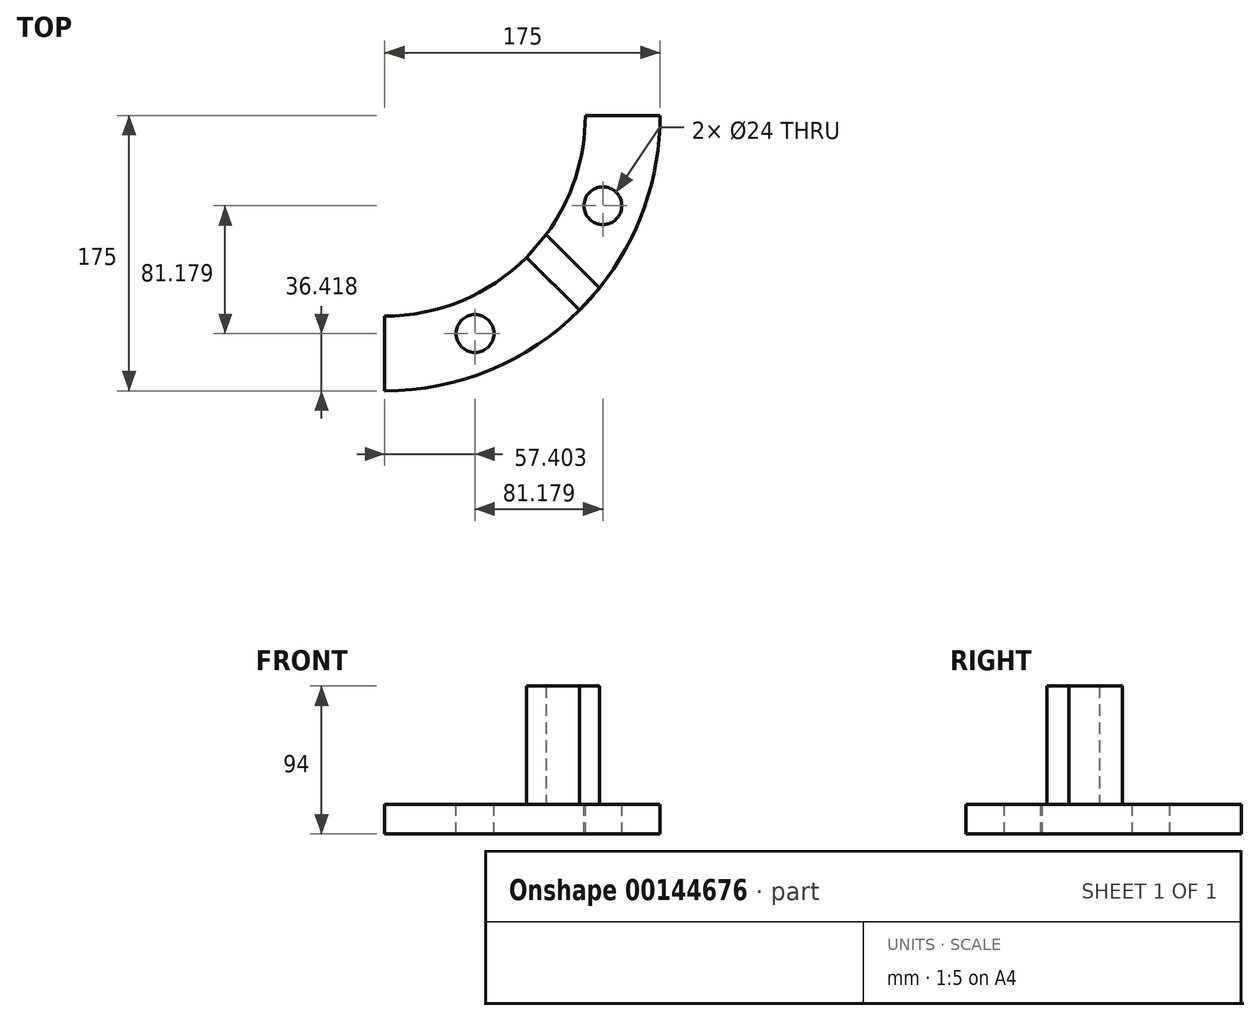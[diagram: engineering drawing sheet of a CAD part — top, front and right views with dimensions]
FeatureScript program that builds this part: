
annotation { "Feature Type Name" : "Feature", "Feature Type Description" : "" }
export const myFeature = defineFeature(function(context is Context, id is Id, definition is map)
    precondition{}
    {
        {
            var Q0;
            Q0=qCreatedBy(makeId("Top.planeOp"),FACE);
            var sketch = newSketch(context, id + "F0", { "sketchPlane" : qUnion([Q0])});
            skArc(sketch, "E0", {"start": v(0, -127.5) * mm, "mid": v(90.16, -90.16) * mm, "end": v(127.5, 0) * mm});
            skArc(sketch, "E1", {"start": v(0, -175) * mm, "mid": v(123.74, -123.74) * mm, "end": v(175, 0) * mm});
            skLineSegment(sketch, "E2", {"start": v(0, 175) * mm, "end": v(0, 0) * mm});
            skLineSegment(sketch, "E3", {"start": v(0, 0) * mm, "end": v(78.54, -189.6) * mm, "construction": true});
            skCircle(sketch, "E4", {"center": v(0, 0) * mm, "radius": 150 * mm, "construction": true});
            skLineSegment(sketch, "E5", {"start": v(0, 0) * mm, "end": v(178.9, -74.1) * mm, "construction": true});
            skLineSegment(sketch, "E6", {"start": v(127.5, 0) * mm, "end": v(191.85, 0) * mm});
            skCircle(sketch, "E7", {"center": v(57.4, -138.58) * mm, "radius": 12 * mm});
            skCircle(sketch, "E8", {"center": v(138.58, -57.4) * mm, "radius": 12 * mm});
            skLineSegment(sketch, "E9", {"start": v(0, 0) * mm, "end": v(154.75, -154.75) * mm});
            skLineSegment(sketch, "E10.trimOffspring", {"start": v(0, -127.5) * mm, "end": v(0, -175) * mm});
            skSolve(sketch);
        }
        {
            var Q0;
            Q0 = qSketchRegion(id + "F0", true);
            extrude(context, id + "F1", {"entities" : qUnion([Q0]), "oppositeDirection" : true, "depth" : 19 * mm});
        }
        {
            var Q0;
            Q0=makeQuery(id+"F0.imprint","IMPRINT",FACE,{"disambiguationData":[TD([[makeQuery(id+"F0.imprint","IMPRINT",EDGE,{"derivedFrom":sQuery(id+"F0.wireOp",EDGE,"E8")}),-1.0]])]});
            var sketch = newSketch(context, id + "F2", { "sketchPlane" : qUnion([Q0])});
            skLineSegment(sketch, "E11.0", {"start": v(90.16, -90.16) * mm, "end": v(123.74, -123.74) * mm});
            skLineSegment(sketch, "E12.0", {"start": v(102.58, -75.71) * mm, "end": v(136.45, -109.58) * mm});
            skArc(sketch, "E13.0", {"start": v(0, -127.5) * mm, "mid": v(90.16, -90.16) * mm, "end": v(127.5, 0) * mm, "construction": true});
            skArc(sketch, "E14.0", {"start": v(0, -175) * mm, "mid": v(123.74, -123.74) * mm, "end": v(175, 0) * mm, "construction": true});
            skPoint(sketch, "E15.orphan", {"position": v(154.75, -154.75) * mm});
            skLineSegment(sketch, "E16", {"start": v(90.16, -90.16) * mm, "end": v(102.58, -75.71) * mm});
            skLineSegment(sketch, "E17", {"start": v(136.45, -109.58) * mm, "end": v(123.74, -123.74) * mm});
            skSolve(sketch);
        }
        {
            var Q0;
            Q0 = qSketchRegion(id + "F2", true);
            extrude(context, id + "F3", {"entities" : qUnion([Q0]), "operationType" : NewBodyOperationType.ADD, "depth" : 75 * mm});
        }
    });
